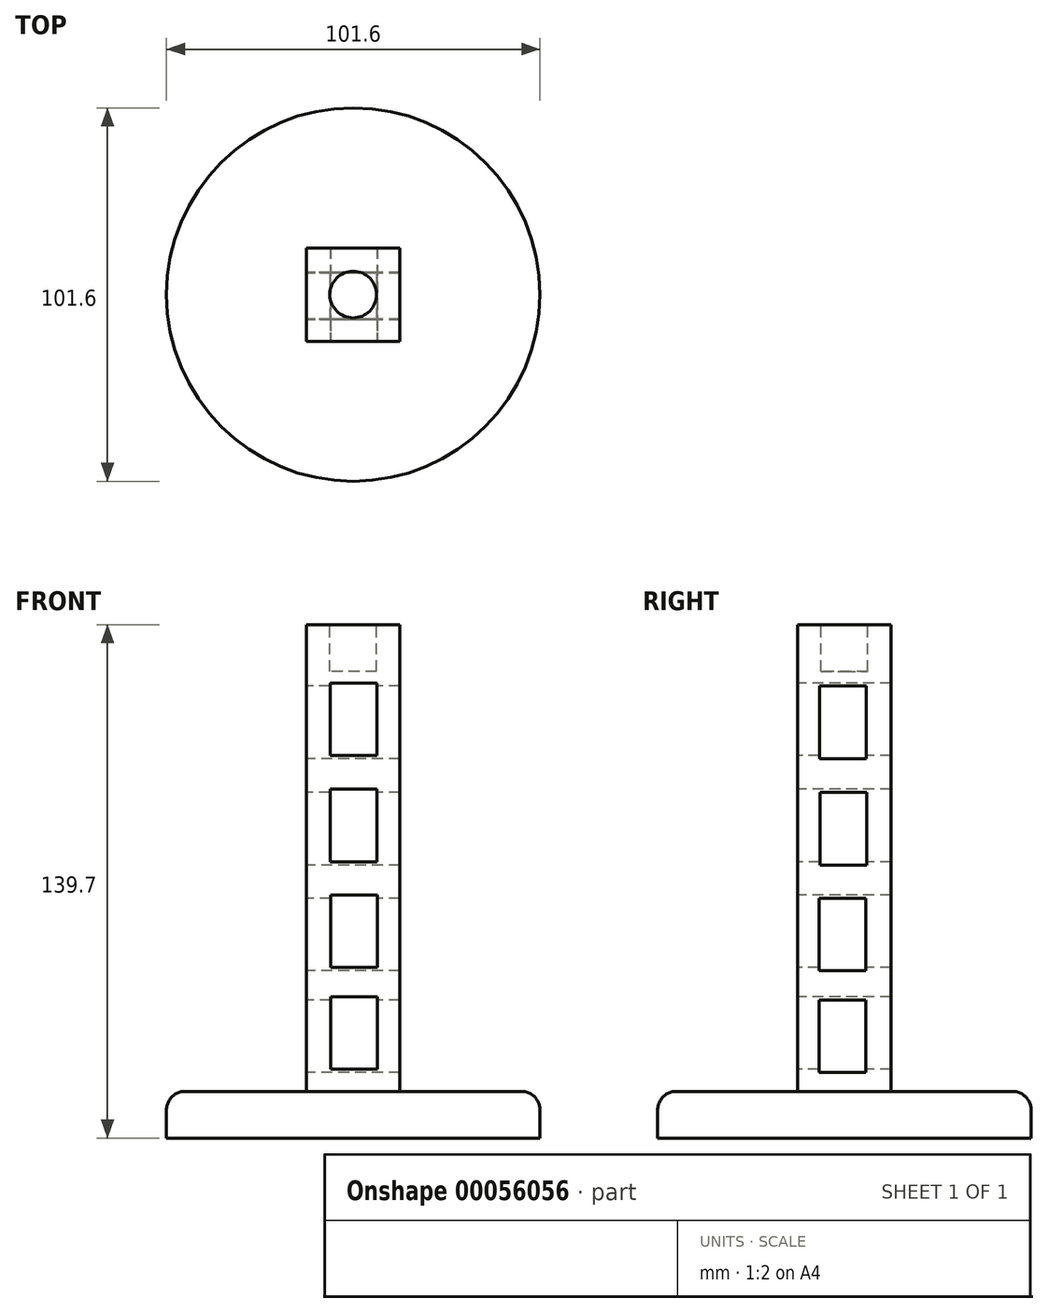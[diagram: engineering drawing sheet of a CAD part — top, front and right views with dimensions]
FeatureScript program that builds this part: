
annotation { "Feature Type Name" : "Feature", "Feature Type Description" : "" }
export const myFeature = defineFeature(function(context is Context, id is Id, definition is map)
    precondition{}
    {
        {
            var Q0;
            Q0=qCreatedBy(makeId("Top.planeOp"),FACE);
            var sketch = newSketch(context, id + "F0", { "sketchPlane" : qUnion([Q0])});
            skCircle(sketch, "E0", {"center": v(0, 0) * mm, "radius": 50.8 * mm});
            skSolve(sketch);
        }
        {
            var Q0;
            Q0 = qSketchRegion(id + "F0", true);
            extrude(context, id + "F1", {"entities" : qUnion([Q0]), "depth" : 12.7 * mm});
        }
        {
            var Q0;
            Q0=makeQuery(id+"F1.opExtrude","CAP_FACE",FACE,{"disambiguationData":[OSD([sQuery(id+"F0.wireOp",EDGE,"E0")])],"isStart":false});
            var sketch = newSketch(context, id + "F2", { "sketchPlane" : qUnion([Q0])});
            skLineSegment(sketch, "E1.rect.bottom", {"start": v(12.7, 12.7) * mm, "end": v(-12.7, 12.7) * mm});
            skLineSegment(sketch, "E1.rect.top", {"start": v(12.7, -12.7) * mm, "end": v(-12.7, -12.7) * mm});
            skLineSegment(sketch, "E1.rect.left", {"start": v(12.7, 12.7) * mm, "end": v(12.7, -12.7) * mm});
            skLineSegment(sketch, "E1.rect.right", {"start": v(-12.7, 12.7) * mm, "end": v(-12.7, -12.7) * mm});
            skPoint(sketch, "E1.rect.middle", {"position": v(0, 0) * mm});
            skSolve(sketch);
        }
        {
            var Q0;
            Q0=makeQuery(id+"F2.imprint","IMPRINT",FACE,{"disambiguationData":[TD([[makeQuery(id+"F2.imprint","IMPRINT",EDGE,{"derivedFrom":sQuery(id+"F2.wireOp",EDGE,"E1.rect.bottom")}),1.0]])]});
            extrude(context, id + "F3", {"entities" : qUnion([Q0]), "operationType" : NewBodyOperationType.ADD, "depth" : 127 * mm});
        }
        {
            var Q0;
            Q0=makeQuery(id+"F3.opExtrude","SWEPT_FACE",FACE,{"disambiguationData":[OSD([sQuery(id+"F2.wireOp",EDGE,"E1.rect.top")])]});
            var sketch = newSketch(context, id + "F4", { "sketchPlane" : qUnion([Q0])});
            skLineSegment(sketch, "E2.rect.bottom", {"start": v(6.45, 123.82) * mm, "end": v(-6.25, 123.82) * mm});
            skLineSegment(sketch, "E2.rect.top", {"start": v(6.45, 104.1) * mm, "end": v(-6.25, 104.1) * mm});
            skLineSegment(sketch, "E2.rect.left", {"start": v(6.45, 123.82) * mm, "end": v(6.45, 104.1) * mm});
            skLineSegment(sketch, "E2.rect.right", {"start": v(-6.25, 123.82) * mm, "end": v(-6.25, 104.1) * mm});
            skPoint(sketch, "E2.rect.middle", {"position": v(0.1, 113.96) * mm});
            skPoint(sketch, "E3.orphan", {"position": v(0, 139.7) * mm});
            skLineSegment(sketch, "E4.rect.top", {"start": v(6.39, 75.17) * mm, "end": v(-6.31, 75.17) * mm});
            skLineSegment(sketch, "E4.rect.bottom", {"start": v(6.39, 94.9) * mm, "end": v(-6.31, 94.9) * mm});
            skLineSegment(sketch, "E4.rect.left", {"start": v(6.39, 94.9) * mm, "end": v(6.39, 75.17) * mm});
            skLineSegment(sketch, "E4.rect.right", {"start": v(-6.31, 94.9) * mm, "end": v(-6.31, 75.17) * mm});
            skPoint(sketch, "E4.rect.middle", {"position": v(0.04, 85.04) * mm});
            skLineSegment(sketch, "E5.rect.top", {"start": v(6.62, 46.4) * mm, "end": v(-6.08, 46.4) * mm});
            skLineSegment(sketch, "E5.rect.bottom", {"start": v(6.62, 66.12) * mm, "end": v(-6.08, 66.12) * mm});
            skLineSegment(sketch, "E5.rect.left", {"start": v(6.62, 66.12) * mm, "end": v(6.62, 46.4) * mm});
            skLineSegment(sketch, "E5.rect.right", {"start": v(-6.08, 66.12) * mm, "end": v(-6.08, 46.4) * mm});
            skPoint(sketch, "E5.rect.middle", {"position": v(0.27, 56.26) * mm});
            skLineSegment(sketch, "E6.rect.top", {"start": v(6.62, 18.7) * mm, "end": v(-6.08, 18.7) * mm});
            skLineSegment(sketch, "E6.rect.bottom", {"start": v(6.62, 38.44) * mm, "end": v(-6.08, 38.44) * mm});
            skLineSegment(sketch, "E6.rect.left", {"start": v(6.62, 38.44) * mm, "end": v(6.62, 18.7) * mm});
            skLineSegment(sketch, "E6.rect.right", {"start": v(-6.08, 38.44) * mm, "end": v(-6.08, 18.7) * mm});
            skPoint(sketch, "E6.rect.middle", {"position": v(0.27, 28.57) * mm});
            skSolve(sketch);
        }
        {
            var Q0;
            Q0 = qSketchRegion(id + "F4", true);
            extrude(context, id + "F5", {"entities" : qUnion([Q0]), "operationType" : NewBodyOperationType.REMOVE, "oppositeDirection" : true, "depth" : 25.4 * mm});
        }
        {
            var Q0;
            Q0=makeQuery(id+"F3.opExtrude","SWEPT_FACE",FACE,{"disambiguationData":[OSD([sQuery(id+"F2.wireOp",EDGE,"E1.rect.right")])]});
            var sketch = newSketch(context, id + "F6", { "sketchPlane" : qUnion([Q0])});
            skLineSegment(sketch, "E7.rect.bottom", {"start": v(6.75, 122.96) * mm, "end": v(-5.95, 122.96) * mm});
            skLineSegment(sketch, "E7.rect.top", {"start": v(6.75, 103.23) * mm, "end": v(-5.95, 103.23) * mm});
            skLineSegment(sketch, "E7.rect.left", {"start": v(6.75, 122.96) * mm, "end": v(6.75, 103.23) * mm});
            skLineSegment(sketch, "E7.rect.right", {"start": v(-5.95, 122.96) * mm, "end": v(-5.95, 103.23) * mm});
            skPoint(sketch, "E7.rect.middle", {"position": v(0.4, 113.1) * mm});
            skPoint(sketch, "E8.orphan", {"position": v(0.3, 138.83) * mm});
            skLineSegment(sketch, "E9.rect.top", {"start": v(6.69, 74.3) * mm, "end": v(-6.01, 74.3) * mm});
            skLineSegment(sketch, "E9.rect.bottom", {"start": v(6.69, 94.04) * mm, "end": v(-6.01, 94.04) * mm});
            skLineSegment(sketch, "E9.rect.left", {"start": v(6.69, 94.04) * mm, "end": v(6.69, 74.3) * mm});
            skLineSegment(sketch, "E9.rect.right", {"start": v(-6.01, 94.04) * mm, "end": v(-6.01, 74.3) * mm});
            skPoint(sketch, "E9.rect.middle", {"position": v(0.34, 84.17) * mm});
            skLineSegment(sketch, "E10.rect.top", {"start": v(6.92, 45.53) * mm, "end": v(-5.78, 45.53) * mm});
            skLineSegment(sketch, "E10.rect.bottom", {"start": v(6.92, 65.26) * mm, "end": v(-5.78, 65.26) * mm});
            skLineSegment(sketch, "E10.rect.left", {"start": v(6.92, 65.26) * mm, "end": v(6.92, 45.53) * mm});
            skLineSegment(sketch, "E10.rect.right", {"start": v(-5.78, 65.26) * mm, "end": v(-5.78, 45.53) * mm});
            skPoint(sketch, "E10.rect.middle", {"position": v(0.57, 55.4) * mm});
            skLineSegment(sketch, "E11.rect.top", {"start": v(6.92, 17.84) * mm, "end": v(-5.78, 17.84) * mm});
            skLineSegment(sketch, "E11.rect.bottom", {"start": v(6.92, 37.57) * mm, "end": v(-5.78, 37.57) * mm});
            skLineSegment(sketch, "E11.rect.left", {"start": v(6.92, 37.57) * mm, "end": v(6.92, 17.84) * mm});
            skLineSegment(sketch, "E11.rect.right", {"start": v(-5.78, 37.57) * mm, "end": v(-5.78, 17.84) * mm});
            skPoint(sketch, "E11.rect.middle", {"position": v(0.57, 27.7) * mm});
            skSolve(sketch);
        }
        {
            var Q0;
            Q0 = qSketchRegion(id + "F6", true);
            extrude(context, id + "F7", {"entities" : qUnion([Q0]), "operationType" : NewBodyOperationType.REMOVE, "oppositeDirection" : true, "depth" : 25.4 * mm});
        }
        {
            var Q0;
            Q0=makeQuery(id+"F3.opExtrude","CAP_FACE",FACE,{"disambiguationData":[OSD([sQuery(id+"F2.wireOp",EDGE,"E1.rect.bottom"),sQuery(id+"F2.wireOp",EDGE,"E1.rect.top"),sQuery(id+"F2.wireOp",EDGE,"E1.rect.left"),sQuery(id+"F2.wireOp",EDGE,"E1.rect.right")])],"isStart":false});
            var sketch = newSketch(context, id + "F8", { "sketchPlane" : qUnion([Q0])});
            skCircle(sketch, "E12", {"center": v(0, 0) * mm, "radius": 6.35 * mm});
            skSolve(sketch);
        }
        {
            var Q0;
            Q0 = qSketchRegion(id + "F8", true);
            extrude(context, id + "F9", {"entities" : qUnion([Q0]), "operationType" : NewBodyOperationType.REMOVE, "oppositeDirection" : true, "depth" : 12.7 * mm});
        }
        {
            var Q0;
            Q0=makeQuery(id+"F1.opExtrude","CAP_EDGE",EDGE,{"disambiguationData":[OSD([sQuery(id+"F0.wireOp",EDGE,"E0")])],"isStart":false});
            fillet(context, id + "F10", {"entities" : qUnion([Q0]), "radius" : 5.08 * mm, "tangentPropagation" : true, "allowEdgeOverflow" : false});
        }
    });
